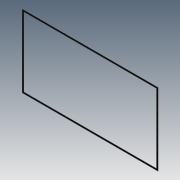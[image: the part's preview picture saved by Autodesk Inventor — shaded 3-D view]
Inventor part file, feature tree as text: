
AUTODESK INVENTOR PART (.ipt)
format: ipt  version: 2012 (Build 160160000, 160)  size: 73,728 bytes
history: native  units: in
note: dims shown in document units (in); Inventor stores cm internally (conversion verified against a paired STEP export)
features: extrude x1, sketch x1
ambient origin geometry x8: Origin, YZ Plane, XZ Plane, XY Plane, X Axis, Y Axis, Z Axis, Center Point
bodies: Solid1 (feature_tree)
feature tree (2):
  extrude  "Extrusion1"  Depth=47.0in
  sketch  "Sketch1"  dims[d0=88.0in d1=47.0in d2=1.0in d3=0.0625in d4=0.0in]
